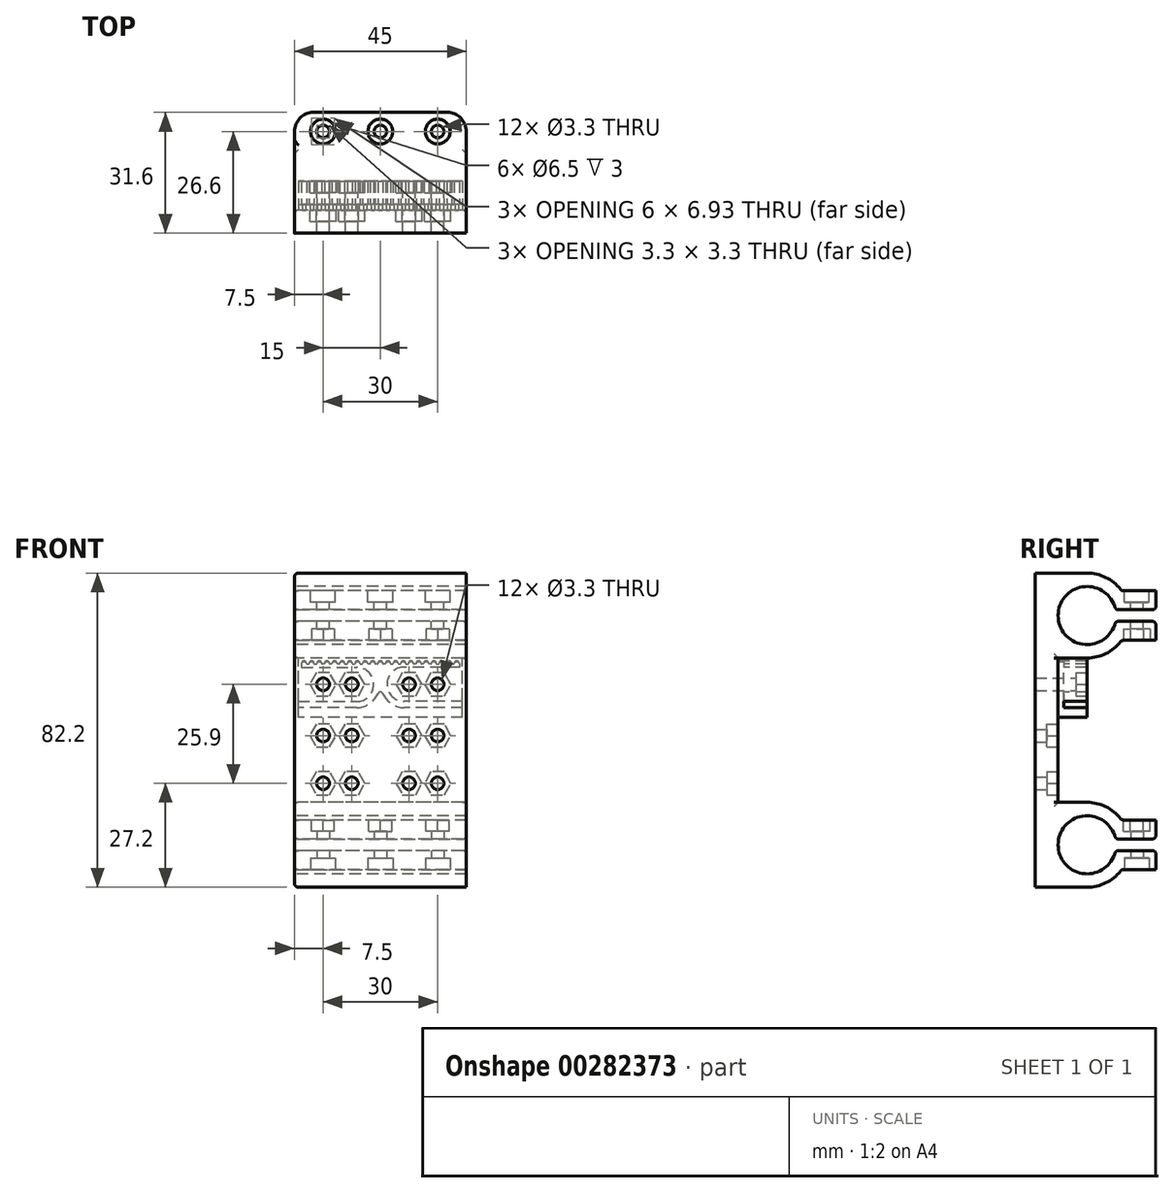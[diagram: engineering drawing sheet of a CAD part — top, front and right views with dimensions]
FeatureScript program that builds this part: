
annotation { "Feature Type Name" : "Feature", "Feature Type Description" : "" }
export const myFeature = defineFeature(function(context is Context, id is Id, definition is map)
    precondition{}
    {
        {
            var Q0;
            Q0=qCreatedBy(makeId("Right.planeOp"),FACE);
            var sketch = newSketch(context, id + "F0", { "sketchPlane" : qUnion([Q0])});
            skLineSegment(sketch, "E0.bottom", {"start": v(0, 0) * mm, "end": v(13.6, 0) * mm});
            skLineSegment(sketch, "E0.top", {"start": v(0, 82.2) * mm, "end": v(13.6, 82.2) * mm});
            skLineSegment(sketch, "E0.left", {"start": v(0, 0) * mm, "end": v(0, 82.2) * mm});
            skLineSegment(sketch, "E0.right", {"start": v(6, 22.2) * mm, "end": v(6, 60) * mm});
            skArc(sketch, "E1", {"start": v(21.05, 72.6) * mm, "mid": v(6, 71.1) * mm, "end": v(21.05, 69.6) * mm});
            skArc(sketch, "E2", {"start": v(21.05, 12.6) * mm, "mid": v(6, 11.1) * mm, "end": v(21.05, 9.6) * mm});
            skLineSegment(sketch, "E3", {"start": v(13.6, 71.1) * mm, "end": v(13.6, 11.1) * mm, "construction": true});
            skLineSegment(sketch, "E4", {"start": v(6, 41.1) * mm, "end": v(13.6, 41.1) * mm, "construction": true});
            skArc(sketch, "E5", {"start": v(13.6, 60) * mm, "mid": v(18.65, 61.22) * mm, "end": v(22.6, 64.6) * mm});
            skArc(sketch, "E6", {"start": v(13.6, 0) * mm, "mid": v(18.65, 1.22) * mm, "end": v(22.6, 4.6) * mm});
            skPoint(sketch, "E7.orphan", {"position": v(6, 82.2) * mm});
            skPoint(sketch, "E8.orphan", {"position": v(6, 0) * mm});
            skLineSegment(sketch, "E9", {"start": v(13.6, 22.2) * mm, "end": v(6, 22.2) * mm});
            skLineSegment(sketch, "E10", {"start": v(13.6, 60) * mm, "end": v(6, 60) * mm});
            skLineSegment(sketch, "E11", {"start": v(13.6, 11.1) * mm, "end": v(31.6, 11.1) * mm, "construction": true});
            skLineSegment(sketch, "E12", {"start": v(13.6, 71.1) * mm, "end": v(31.6, 71.1) * mm, "construction": true});
            skLineSegment(sketch, "E13.0", {"start": v(21.05, 9.6) * mm, "end": v(31.6, 9.6) * mm});
            skLineSegment(sketch, "E14.0", {"start": v(21.05, 12.6) * mm, "end": v(31.6, 12.6) * mm});
            skLineSegment(sketch, "E15.0", {"start": v(22.6, 4.6) * mm, "end": v(31.6, 4.6) * mm});
            skLineSegment(sketch, "E16.0", {"start": v(22.6, 17.6) * mm, "end": v(31.6, 17.6) * mm});
            skLineSegment(sketch, "E17", {"start": v(31.6, 17.6) * mm, "end": v(31.6, 12.6) * mm});
            skLineSegment(sketch, "E18", {"start": v(31.6, 9.6) * mm, "end": v(31.6, 4.6) * mm});
            skLineSegment(sketch, "E19", {"start": v(31.6, 12.6) * mm, "end": v(31.6, 11.1) * mm, "construction": true});
            skLineSegment(sketch, "E20", {"start": v(31.6, 9.6) * mm, "end": v(31.6, 11.1) * mm, "construction": true});
            skArc(sketch, "E21.trimOffspring", {"start": v(22.6, 17.6) * mm, "mid": v(18.65, 20.98) * mm, "end": v(13.6, 22.2) * mm});
            skLineSegment(sketch, "E22.0", {"start": v(21.05, 69.6) * mm, "end": v(31.6, 69.6) * mm});
            skLineSegment(sketch, "E23.0", {"start": v(21.05, 72.6) * mm, "end": v(31.6, 72.6) * mm});
            skLineSegment(sketch, "E24.0", {"start": v(22.6, 77.6) * mm, "end": v(31.6, 77.6) * mm});
            skLineSegment(sketch, "E25.0", {"start": v(22.6, 64.6) * mm, "end": v(31.6, 64.6) * mm});
            skLineSegment(sketch, "E26", {"start": v(31.6, 64.6) * mm, "end": v(31.6, 69.6) * mm});
            skLineSegment(sketch, "E27", {"start": v(31.6, 77.6) * mm, "end": v(31.6, 72.6) * mm});
            skLineSegment(sketch, "E28", {"start": v(31.6, 69.6) * mm, "end": v(31.6, 71.1) * mm, "construction": true});
            skLineSegment(sketch, "E29", {"start": v(31.6, 72.6) * mm, "end": v(31.6, 71.1) * mm, "construction": true});
            skArc(sketch, "E30.trimOffspring", {"start": v(22.6, 77.6) * mm, "mid": v(18.65, 80.98) * mm, "end": v(13.6, 82.2) * mm});
            skSolve(sketch);
        }
        {
            var Q0;
            Q0=qSketchRegion(id+"F0",true);
            extrude(context, id + "F1", {"entities" : qUnion([Q0]), "depth" : 45 * mm});
        }
        {
            var Q0;
            Q0=makeQuery(id+"F1.opExtrude","CAP_EDGE",EDGE,{"disambiguationData":[OSD([sQuery(id+"F0.wireOp",EDGE,"E0.right")])],"isStart":true});
            var Q1;
            Q1=makeQuery(id+"F1.opExtrude","CAP_EDGE",EDGE,{"disambiguationData":[OSD([sQuery(id+"F0.wireOp",EDGE,"E0.right")])],"isStart":false});
            fillet(context, id + "F2", {"entities" : qUnion([Q0, Q1]), "radius" : 1 * mm, "tangentPropagation" : true, "allowEdgeOverflow" : false});
        }
        {
            var Q0;
            Q0=makeQuery(id+"F1.opExtrude","SWEPT_FACE",FACE,{"disambiguationData":[OSD([sQuery(id+"F0.wireOp",EDGE,"E0.right")])]});
            var sketch = newSketch(context, id + "F3", { "sketchPlane" : qUnion([Q0])});
            skLineSegment(sketch, "E31.bottom", {"start": v(-43.15, 57.6) * mm, "end": v(-28.75, 57.6) * mm});
            skLineSegment(sketch, "E31.top", {"start": v(-44, 48.6) * mm, "end": v(-28.75, 48.6) * mm});
            skLineSegment(sketch, "E31.left", {"start": v(-44, 60) * mm, "end": v(-44, 48.6) * mm});
            skLineSegment(sketch, "E31.right", {"start": v(-28.75, 57.6) * mm, "end": v(-28.75, 48.6) * mm, "construction": true});
            skLineSegment(sketch, "E32.bottom", {"start": v(-1, 48.6) * mm, "end": v(-16.25, 48.6) * mm});
            skLineSegment(sketch, "E32.top", {"start": v(-1.85, 57.6) * mm, "end": v(-16.25, 57.6) * mm});
            skLineSegment(sketch, "E32.left", {"start": v(-1, 48.6) * mm, "end": v(-1, 60) * mm});
            skLineSegment(sketch, "E32.right", {"start": v(-16.25, 48.6) * mm, "end": v(-16.25, 57.6) * mm, "construction": true});
            skArc(sketch, "E33", {"start": v(-28.75, 48.6) * mm, "mid": v(-24.25, 53.1) * mm, "end": v(-28.75, 57.6) * mm});
            skArc(sketch, "E34", {"start": v(-16.25, 57.6) * mm, "mid": v(-20.75, 53.1) * mm, "end": v(-16.25, 48.6) * mm});
            skLineSegment(sketch, "E35", {"start": v(-28.75, 53.1) * mm, "end": v(-16.25, 53.1) * mm, "construction": true});
            skLineSegment(sketch, "E36", {"start": v(-22.5, 60) * mm, "end": v(-22.5, 53.1) * mm, "construction": true});
            skLineSegment(sketch, "E37.bottom", {"start": v(-44, 60) * mm, "end": v(-1, 60) * mm});
            skLineSegment(sketch, "E37.top", {"start": v(-44, 59.2) * mm, "end": v(-1, 59.2) * mm, "construction": true});
            skLineSegment(sketch, "E38.bottom", {"start": v(-44, 47) * mm, "end": v(-28.75, 47) * mm});
            skLineSegment(sketch, "E38.top", {"start": v(-44, 44.5) * mm, "end": v(-1, 44.5) * mm});
            skLineSegment(sketch, "E38.left", {"start": v(-44, 47) * mm, "end": v(-44, 44.5) * mm});
            skLineSegment(sketch, "E39", {"start": v(-1, 47) * mm, "end": v(-1, 44.5) * mm});
            skLineSegment(sketch, "E40", {"start": v(-25.5, 58.45) * mm, "end": v(-25.25, 58.45) * mm});
            skLineSegment(sketch, "E41", {"start": v(-20.5, 60) * mm, "end": v(-20.5, 53.1) * mm, "construction": true});
            skLineSegment(sketch, "E42", {"start": v(-24.5, 60) * mm, "end": v(-24.5, 53.1) * mm, "construction": true});
            skLineSegment(sketch, "E43", {"start": v(-25.15, 58.55) * mm, "end": v(-19.85, 58.55) * mm, "construction": true});
            skArc(sketch, "E44", {"start": v(-23.85, 58.55) * mm, "mid": v(-24.5, 59.2) * mm, "end": v(-25.15, 58.55) * mm});
            skArc(sketch, "E45", {"start": v(-21.85, 58.55) * mm, "mid": v(-22.5, 59.2) * mm, "end": v(-23.15, 58.55) * mm});
            skArc(sketch, "E46", {"start": v(-19.85, 58.55) * mm, "mid": v(-20.5, 59.2) * mm, "end": v(-21.15, 58.55) * mm});
            skLineSegment(sketch, "E47", {"start": v(-19.85, 58.55) * mm, "end": v(-19.85, 58.55) * mm});
            skLineSegment(sketch, "E48", {"start": v(-21.15, 58.55) * mm, "end": v(-21.15, 58.55) * mm});
            skLineSegment(sketch, "E49", {"start": v(-21.85, 58.55) * mm, "end": v(-21.85, 58.55) * mm});
            skLineSegment(sketch, "E50", {"start": v(-23.15, 58.55) * mm, "end": v(-23.15, 58.55) * mm});
            skLineSegment(sketch, "E51", {"start": v(-23.85, 58.55) * mm, "end": v(-23.85, 58.55) * mm});
            skLineSegment(sketch, "E52", {"start": v(-25.15, 58.55) * mm, "end": v(-25.15, 58.55) * mm});
            skLineSegment(sketch, "E53.trimOffspring", {"start": v(-21.75, 58.45) * mm, "end": v(-21.25, 58.45) * mm});
            skLineSegment(sketch, "E54.trimOffspring", {"start": v(-23.75, 58.45) * mm, "end": v(-23.25, 58.45) * mm});
            skLineSegment(sketch, "E55.trimOffspring", {"start": v(-19.75, 58.45) * mm, "end": v(-19.5, 58.45) * mm});
            skPoint(sketch, "E56.visualSharp", {"position": v(-23.85, 58.45) * mm});
            skArc(sketch, "E56.filletArc", {"start": v(-23.85, 58.55) * mm, "mid": v(-23.82, 58.48) * mm, "end": v(-23.75, 58.45) * mm});
            skPoint(sketch, "E57.visualSharp", {"position": v(-23.15, 58.45) * mm});
            skArc(sketch, "E57.filletArc", {"start": v(-23.25, 58.45) * mm, "mid": v(-23.18, 58.48) * mm, "end": v(-23.15, 58.55) * mm});
            skPoint(sketch, "E58.visualSharp", {"position": v(-21.85, 58.45) * mm});
            skArc(sketch, "E58.filletArc", {"start": v(-21.85, 58.55) * mm, "mid": v(-21.82, 58.48) * mm, "end": v(-21.75, 58.45) * mm});
            skPoint(sketch, "E59.visualSharp", {"position": v(-21.15, 58.45) * mm});
            skArc(sketch, "E59.filletArc", {"start": v(-21.25, 58.45) * mm, "mid": v(-21.18, 58.48) * mm, "end": v(-21.15, 58.55) * mm});
            skPoint(sketch, "E60.visualSharp", {"position": v(-25.15, 58.45) * mm});
            skArc(sketch, "E60.filletArc", {"start": v(-25.25, 58.45) * mm, "mid": v(-25.18, 58.48) * mm, "end": v(-25.15, 58.55) * mm});
            skPoint(sketch, "E61.visualSharp", {"position": v(-19.85, 58.45) * mm});
            skArc(sketch, "E61.filletArc", {"start": v(-19.85, 58.55) * mm, "mid": v(-19.82, 58.48) * mm, "end": v(-19.75, 58.45) * mm});
            skLineSegment(sketch, "E62", {"start": v(-25.5, 60) * mm, "end": v(-25.5, 53.1) * mm, "construction": true});
            skLineSegment(sketch, "E63", {"start": v(-19.5, 60) * mm, "end": v(-19.5, 53.1) * mm, "construction": true});
            skLineSegment(sketch, "E64.MirrorCS", {"start": v(-25.5, 58.45) * mm, "end": v(-25.75, 58.45) * mm});
            skPoint(sketch, "E65.MirrorP", {"position": v(-25.85, 58.45) * mm});
            skArc(sketch, "E66.MirrorCS", {"start": v(-25.75, 58.45) * mm, "mid": v(-25.82, 58.48) * mm, "end": v(-25.85, 58.55) * mm});
            skArc(sketch, "E67.MirrorCS", {"start": v(-27.15, 58.55) * mm, "mid": v(-26.5, 59.2) * mm, "end": v(-25.85, 58.55) * mm});
            skArc(sketch, "E68.MirrorCS", {"start": v(-27.15, 58.55) * mm, "mid": v(-27.18, 58.48) * mm, "end": v(-27.25, 58.45) * mm});
            skLineSegment(sketch, "E69.MirrorCS", {"start": v(-27.25, 58.45) * mm, "end": v(-27.75, 58.45) * mm});
            skArc(sketch, "E70.MirrorCS", {"start": v(-27.75, 58.45) * mm, "mid": v(-27.82, 58.48) * mm, "end": v(-27.85, 58.55) * mm});
            skArc(sketch, "E71.MirrorCS", {"start": v(-29.15, 58.55) * mm, "mid": v(-28.5, 59.2) * mm, "end": v(-27.85, 58.55) * mm});
            skArc(sketch, "E72.MirrorCS", {"start": v(-29.15, 58.55) * mm, "mid": v(-29.18, 58.48) * mm, "end": v(-29.25, 58.45) * mm});
            skLineSegment(sketch, "E73.MirrorCS", {"start": v(-29.25, 58.45) * mm, "end": v(-29.75, 58.45) * mm});
            skArc(sketch, "E74.MirrorCS", {"start": v(-29.75, 58.45) * mm, "mid": v(-29.82, 58.48) * mm, "end": v(-29.85, 58.55) * mm});
            skArc(sketch, "E75.MirrorCS", {"start": v(-31.15, 58.55) * mm, "mid": v(-30.5, 59.2) * mm, "end": v(-29.85, 58.55) * mm});
            skArc(sketch, "E76.MirrorCS", {"start": v(-31.15, 58.55) * mm, "mid": v(-31.18, 58.48) * mm, "end": v(-31.25, 58.45) * mm});
            skLineSegment(sketch, "E77.MirrorCS", {"start": v(-31.25, 58.45) * mm, "end": v(-31.5, 58.45) * mm});
            skLineSegment(sketch, "E78.MirrorCS", {"start": v(-19.25, 58.45) * mm, "end": v(-19.5, 58.45) * mm});
            skArc(sketch, "E79.MirrorCS", {"start": v(-19.15, 58.55) * mm, "mid": v(-19.18, 58.48) * mm, "end": v(-19.25, 58.45) * mm});
            skArc(sketch, "E80.MirrorCS", {"start": v(-19.15, 58.55) * mm, "mid": v(-18.5, 59.2) * mm, "end": v(-17.85, 58.55) * mm});
            skArc(sketch, "E81.MirrorCS", {"start": v(-17.75, 58.45) * mm, "mid": v(-17.82, 58.48) * mm, "end": v(-17.85, 58.55) * mm});
            skLineSegment(sketch, "E82.MirrorCS", {"start": v(-17.25, 58.45) * mm, "end": v(-17.75, 58.45) * mm});
            skPoint(sketch, "E83.MirrorP", {"position": v(-17.15, 58.45) * mm});
            skArc(sketch, "E84.MirrorCS", {"start": v(-17.15, 58.55) * mm, "mid": v(-17.18, 58.48) * mm, "end": v(-17.25, 58.45) * mm});
            skArc(sketch, "E85.MirrorCS", {"start": v(-17.15, 58.55) * mm, "mid": v(-16.5, 59.2) * mm, "end": v(-15.85, 58.55) * mm});
            skArc(sketch, "E86.MirrorCS", {"start": v(-15.75, 58.45) * mm, "mid": v(-15.82, 58.48) * mm, "end": v(-15.85, 58.55) * mm});
            skLineSegment(sketch, "E87.MirrorCS", {"start": v(-15.25, 58.45) * mm, "end": v(-15.75, 58.45) * mm});
            skArc(sketch, "E88.MirrorCS", {"start": v(-15.15, 58.55) * mm, "mid": v(-15.18, 58.48) * mm, "end": v(-15.25, 58.45) * mm});
            skArc(sketch, "E89.MirrorCS", {"start": v(-15.15, 58.55) * mm, "mid": v(-14.5, 59.2) * mm, "end": v(-13.85, 58.55) * mm});
            skArc(sketch, "E90.MirrorCS", {"start": v(-13.75, 58.45) * mm, "mid": v(-13.82, 58.48) * mm, "end": v(-13.85, 58.55) * mm});
            skLineSegment(sketch, "E91.MirrorCS", {"start": v(-13.5, 58.45) * mm, "end": v(-13.75, 58.45) * mm});
            skLineSegment(sketch, "E92.MirrorCS", {"start": v(-13.5, 58.45) * mm, "end": v(-13.25, 58.45) * mm});
            skArc(sketch, "E93.MirrorCS", {"start": v(-13.25, 58.45) * mm, "mid": v(-13.18, 58.48) * mm, "end": v(-13.15, 58.55) * mm});
            skArc(sketch, "E94.MirrorCS", {"start": v(-11.85, 58.55) * mm, "mid": v(-12.5, 59.2) * mm, "end": v(-13.15, 58.55) * mm});
            skArc(sketch, "E95.MirrorCS", {"start": v(-11.85, 58.55) * mm, "mid": v(-11.82, 58.48) * mm, "end": v(-11.75, 58.45) * mm});
            skLineSegment(sketch, "E96.MirrorCS", {"start": v(-11.75, 58.45) * mm, "end": v(-11.25, 58.45) * mm});
            skArc(sketch, "E97.MirrorCS", {"start": v(-11.25, 58.45) * mm, "mid": v(-11.18, 58.48) * mm, "end": v(-11.15, 58.55) * mm});
            skArc(sketch, "E98.MirrorCS", {"start": v(-9.85, 58.55) * mm, "mid": v(-10.5, 59.2) * mm, "end": v(-11.15, 58.55) * mm});
            skArc(sketch, "E99.MirrorCS", {"start": v(-9.85, 58.55) * mm, "mid": v(-9.82, 58.48) * mm, "end": v(-9.75, 58.45) * mm});
            skLineSegment(sketch, "E100.MirrorCS", {"start": v(-9.75, 58.45) * mm, "end": v(-9.25, 58.45) * mm});
            skArc(sketch, "E101.MirrorCS", {"start": v(-9.25, 58.45) * mm, "mid": v(-9.18, 58.48) * mm, "end": v(-9.15, 58.55) * mm});
            skArc(sketch, "E102.MirrorCS", {"start": v(-7.85, 58.55) * mm, "mid": v(-8.5, 59.2) * mm, "end": v(-9.15, 58.55) * mm});
            skArc(sketch, "E103.MirrorCS", {"start": v(-7.85, 58.55) * mm, "mid": v(-7.82, 58.48) * mm, "end": v(-7.75, 58.45) * mm});
            skLineSegment(sketch, "E104.MirrorCS", {"start": v(-7.75, 58.45) * mm, "end": v(-7.5, 58.45) * mm});
            skLineSegment(sketch, "E105", {"start": v(-28.75, 53.1) * mm, "end": v(-31.5, 53.1) * mm, "construction": true});
            skLineSegment(sketch, "E106", {"start": v(-31.5, 53.1) * mm, "end": v(-31.5, 60) * mm, "construction": true});
            skLineSegment(sketch, "E107.MirrorCS", {"start": v(-31.75, 58.45) * mm, "end": v(-31.5, 58.45) * mm});
            skArc(sketch, "E108.MirrorCS", {"start": v(-31.85, 58.55) * mm, "mid": v(-31.82, 58.48) * mm, "end": v(-31.75, 58.45) * mm});
            skArc(sketch, "E109.MirrorCS", {"start": v(-31.85, 58.55) * mm, "mid": v(-32.5, 59.2) * mm, "end": v(-33.15, 58.55) * mm});
            skArc(sketch, "E110.MirrorCS", {"start": v(-33.25, 58.45) * mm, "mid": v(-33.18, 58.48) * mm, "end": v(-33.15, 58.55) * mm});
            skLineSegment(sketch, "E111.MirrorCS", {"start": v(-33.75, 58.45) * mm, "end": v(-33.25, 58.45) * mm});
            skArc(sketch, "E112.MirrorCS", {"start": v(-33.85, 58.55) * mm, "mid": v(-33.82, 58.48) * mm, "end": v(-33.75, 58.45) * mm});
            skArc(sketch, "E113.MirrorCS", {"start": v(-33.85, 58.55) * mm, "mid": v(-34.5, 59.2) * mm, "end": v(-35.15, 58.55) * mm});
            skArc(sketch, "E114.MirrorCS", {"start": v(-35.25, 58.45) * mm, "mid": v(-35.18, 58.48) * mm, "end": v(-35.15, 58.55) * mm});
            skLineSegment(sketch, "E115.MirrorCS", {"start": v(-35.75, 58.45) * mm, "end": v(-35.25, 58.45) * mm});
            skArc(sketch, "E116.MirrorCS", {"start": v(-35.85, 58.55) * mm, "mid": v(-35.82, 58.48) * mm, "end": v(-35.75, 58.45) * mm});
            skArc(sketch, "E117.MirrorCS", {"start": v(-35.85, 58.55) * mm, "mid": v(-36.5, 59.2) * mm, "end": v(-37.15, 58.55) * mm});
            skArc(sketch, "E118.MirrorCS", {"start": v(-37.25, 58.45) * mm, "mid": v(-37.18, 58.48) * mm, "end": v(-37.15, 58.55) * mm});
            skLineSegment(sketch, "E119.MirrorCS", {"start": v(-37.5, 58.45) * mm, "end": v(-37.25, 58.45) * mm});
            skLineSegment(sketch, "E120.MirrorCS", {"start": v(-37.5, 58.45) * mm, "end": v(-37.75, 58.45) * mm});
            skArc(sketch, "E121.MirrorCS", {"start": v(-37.75, 58.45) * mm, "mid": v(-37.82, 58.48) * mm, "end": v(-37.85, 58.55) * mm});
            skArc(sketch, "E122.MirrorCS", {"start": v(-39.15, 58.55) * mm, "mid": v(-38.5, 59.2) * mm, "end": v(-37.85, 58.55) * mm});
            skArc(sketch, "E123.MirrorCS", {"start": v(-39.15, 58.55) * mm, "mid": v(-39.18, 58.48) * mm, "end": v(-39.25, 58.45) * mm});
            skLineSegment(sketch, "E124.MirrorCS", {"start": v(-39.25, 58.45) * mm, "end": v(-39.75, 58.45) * mm});
            skArc(sketch, "E125.MirrorCS", {"start": v(-39.75, 58.45) * mm, "mid": v(-39.82, 58.48) * mm, "end": v(-39.85, 58.55) * mm});
            skArc(sketch, "E126.MirrorCS", {"start": v(-41.15, 58.55) * mm, "mid": v(-40.5, 59.2) * mm, "end": v(-39.85, 58.55) * mm});
            skArc(sketch, "E127.MirrorCS", {"start": v(-41.15, 58.55) * mm, "mid": v(-41.18, 58.48) * mm, "end": v(-41.25, 58.45) * mm});
            skLineSegment(sketch, "E128.MirrorCS", {"start": v(-41.25, 58.45) * mm, "end": v(-41.75, 58.45) * mm});
            skArc(sketch, "E129.MirrorCS", {"start": v(-41.75, 58.45) * mm, "mid": v(-41.82, 58.48) * mm, "end": v(-41.85, 58.55) * mm});
            skArc(sketch, "E130.MirrorCS", {"start": v(-43.15, 58.55) * mm, "mid": v(-42.5, 59.2) * mm, "end": v(-41.85, 58.55) * mm});
            skLineSegment(sketch, "E131", {"start": v(-16.25, 53.1) * mm, "end": v(-7.5, 53.1) * mm, "construction": true});
            skLineSegment(sketch, "E132", {"start": v(-7.5, 53.1) * mm, "end": v(-7.5, 58.45) * mm, "construction": true});
            skLineSegment(sketch, "E133", {"start": v(-7.5, 60) * mm, "end": v(-7.5, 58.45) * mm, "construction": true});
            skLineSegment(sketch, "E134.MirrorCS", {"start": v(-7.25, 58.45) * mm, "end": v(-7.5, 58.45) * mm});
            skArc(sketch, "E135.MirrorCS", {"start": v(-7.15, 58.55) * mm, "mid": v(-7.18, 58.48) * mm, "end": v(-7.25, 58.45) * mm});
            skArc(sketch, "E136.MirrorCS", {"start": v(-7.15, 58.55) * mm, "mid": v(-6.5, 59.2) * mm, "end": v(-5.85, 58.55) * mm});
            skArc(sketch, "E137.MirrorCS", {"start": v(-5.75, 58.45) * mm, "mid": v(-5.82, 58.48) * mm, "end": v(-5.85, 58.55) * mm});
            skLineSegment(sketch, "E138.MirrorCS", {"start": v(-5.25, 58.45) * mm, "end": v(-5.75, 58.45) * mm});
            skArc(sketch, "E139.MirrorCS", {"start": v(-5.15, 58.55) * mm, "mid": v(-5.18, 58.48) * mm, "end": v(-5.25, 58.45) * mm});
            skArc(sketch, "E140.MirrorCS", {"start": v(-5.15, 58.55) * mm, "mid": v(-4.5, 59.2) * mm, "end": v(-3.85, 58.55) * mm});
            skArc(sketch, "E141.MirrorCS", {"start": v(-3.75, 58.45) * mm, "mid": v(-3.82, 58.48) * mm, "end": v(-3.85, 58.55) * mm});
            skLineSegment(sketch, "E142.MirrorCS", {"start": v(-3.25, 58.45) * mm, "end": v(-3.75, 58.45) * mm});
            skArc(sketch, "E143.MirrorCS", {"start": v(-3.15, 58.55) * mm, "mid": v(-3.18, 58.48) * mm, "end": v(-3.25, 58.45) * mm});
            skArc(sketch, "E144.MirrorCS", {"start": v(-3.15, 58.55) * mm, "mid": v(-2.5, 59.2) * mm, "end": v(-1.85, 58.55) * mm});
            skLineSegment(sketch, "E145", {"start": v(-1.85, 58.55) * mm, "end": v(-1.85, 57.6) * mm});
            skLineSegment(sketch, "E146", {"start": v(-43.15, 58.55) * mm, "end": v(-43.15, 57.6) * mm});
            skLineSegment(sketch, "E147", {"start": v(-22.5, 53.1) * mm, "end": v(-22.5, 47) * mm, "construction": true});
            skArc(sketch, "E148.0", {"start": v(-21.82, 50.6) * mm, "mid": v(-19.57, 47.98) * mm, "end": v(-16.25, 47) * mm});
            skArc(sketch, "E149.0", {"start": v(-28.75, 47) * mm, "mid": v(-25.43, 47.98) * mm, "end": v(-23.18, 50.6) * mm});
            skLineSegment(sketch, "E150.trimOffspring", {"start": v(-16.25, 47) * mm, "end": v(-1, 47) * mm});
            skArc(sketch, "E151", {"start": v(-21.82, 50.6) * mm, "mid": v(-22.5, 51.05) * mm, "end": v(-23.18, 50.6) * mm});
            skLineSegment(sketch, "E152", {"start": v(-28.75, 47) * mm, "end": v(-22.5, 47) * mm, "construction": true});
            skLineSegment(sketch, "E153", {"start": v(-16.25, 47) * mm, "end": v(-22.5, 47) * mm, "construction": true});
            skSolve(sketch);
        }
        {
            var Q0;
            Q0=qSketchRegion(id+"F3",true);
            extrude(context, id + "F4", {"entities" : qUnion([Q0]), "operationType" : NewBodyOperationType.ADD, "depth" : 7.6 * mm});
        }
        {
            var Q0;
            {var subQ0=sQuery(id+"F0.wireOp",EDGE,"E0.right");Q0=makeQuery(id+"F4.boolean.opBoolean","SPLIT",FACE,{"disambiguationData":[TD([makeQuery(id+"F4.opExtrude","SWEPT_FACE",FACE,{"disambiguationData":[OSD([sQuery(id+"F3.wireOp",EDGE,"E31.bottom")])]})])],"derivedFrom":makeQuery(id+"F1.opExtrude","SWEPT_FACE",FACE,{"disambiguationData":[OSD([subQ0])]})});}
            var sketch = newSketch(context, id + "F5", { "sketchPlane" : qUnion([Q0])});
            skLineSegment(sketch, "E154.bottom", {"start": v(-44, 47) * mm, "end": v(-1, 47) * mm});
            skLineSegment(sketch, "E154.top", {"start": v(-44, 59) * mm, "end": v(-1, 59) * mm});
            skLineSegment(sketch, "E154.left", {"start": v(-44, 47) * mm, "end": v(-44, 59) * mm});
            skLineSegment(sketch, "E154.right", {"start": v(-1, 47) * mm, "end": v(-1, 59) * mm});
            skSolve(sketch);
        }
        {
            var Q0;
            Q0=qSketchRegion(id+"F5",true);
            extrude(context, id + "F6", {"entities" : qUnion([Q0]), "operationType" : NewBodyOperationType.ADD, "depth" : 1.5 * mm});
        }
        {
            var Q0;
            Q0=makeQuery(id+"F4.opExtrude","CAP_FACE",FACE,{"disambiguationData":[OSD([sQuery(id+"F3.wireOp",EDGE,"E31.bottom"),sQuery(id+"F3.wireOp",EDGE,"E31.top"),sQuery(id+"F3.wireOp",EDGE,"E31.left"),sQuery(id+"F3.wireOp",EDGE,"E32.bottom"),sQuery(id+"F3.wireOp",EDGE,"E32.top"),sQuery(id+"F3.wireOp",EDGE,"E32.left"),sQuery(id+"F3.wireOp",EDGE,"E33"),sQuery(id+"F3.wireOp",EDGE,"E34"),sQuery(id+"F3.wireOp",EDGE,"E37.bottom"),sQuery(id+"F3.wireOp",EDGE,"E40"),sQuery(id+"F3.wireOp",EDGE,"E44"),sQuery(id+"F3.wireOp",EDGE,"E45"),sQuery(id+"F3.wireOp",EDGE,"E46"),sQuery(id+"F3.wireOp",EDGE,"E53.trimOffspring"),sQuery(id+"F3.wireOp",EDGE,"E54.trimOffspring"),sQuery(id+"F3.wireOp",EDGE,"E55.trimOffspring"),sQuery(id+"F3.wireOp",EDGE,"E56.filletArc"),sQuery(id+"F3.wireOp",EDGE,"E57.filletArc"),sQuery(id+"F3.wireOp",EDGE,"E58.filletArc"),sQuery(id+"F3.wireOp",EDGE,"E59.filletArc"),sQuery(id+"F3.wireOp",EDGE,"E60.filletArc"),sQuery(id+"F3.wireOp",EDGE,"E61.filletArc"),sQuery(id+"F3.wireOp",EDGE,"E64.MirrorCS"),sQuery(id+"F3.wireOp",EDGE,"E66.MirrorCS"),sQuery(id+"F3.wireOp",EDGE,"E67.MirrorCS"),sQuery(id+"F3.wireOp",EDGE,"E68.MirrorCS"),sQuery(id+"F3.wireOp",EDGE,"E69.MirrorCS"),sQuery(id+"F3.wireOp",EDGE,"E70.MirrorCS"),sQuery(id+"F3.wireOp",EDGE,"E71.MirrorCS"),sQuery(id+"F3.wireOp",EDGE,"E72.MirrorCS"),sQuery(id+"F3.wireOp",EDGE,"E73.MirrorCS"),sQuery(id+"F3.wireOp",EDGE,"E74.MirrorCS"),sQuery(id+"F3.wireOp",EDGE,"E75.MirrorCS"),sQuery(id+"F3.wireOp",EDGE,"E76.MirrorCS"),sQuery(id+"F3.wireOp",EDGE,"E77.MirrorCS"),sQuery(id+"F3.wireOp",EDGE,"E78.MirrorCS"),sQuery(id+"F3.wireOp",EDGE,"E79.MirrorCS"),sQuery(id+"F3.wireOp",EDGE,"E80.MirrorCS"),sQuery(id+"F3.wireOp",EDGE,"E81.MirrorCS"),sQuery(id+"F3.wireOp",EDGE,"E82.MirrorCS"),sQuery(id+"F3.wireOp",EDGE,"E84.MirrorCS"),sQuery(id+"F3.wireOp",EDGE,"E85.MirrorCS"),sQuery(id+"F3.wireOp",EDGE,"E86.MirrorCS"),sQuery(id+"F3.wireOp",EDGE,"E87.MirrorCS"),sQuery(id+"F3.wireOp",EDGE,"E88.MirrorCS"),sQuery(id+"F3.wireOp",EDGE,"E89.MirrorCS"),sQuery(id+"F3.wireOp",EDGE,"E90.MirrorCS"),sQuery(id+"F3.wireOp",EDGE,"E91.MirrorCS"),sQuery(id+"F3.wireOp",EDGE,"E92.MirrorCS"),sQuery(id+"F3.wireOp",EDGE,"E93.MirrorCS"),sQuery(id+"F3.wireOp",EDGE,"E94.MirrorCS"),sQuery(id+"F3.wireOp",EDGE,"E95.MirrorCS"),sQuery(id+"F3.wireOp",EDGE,"E96.MirrorCS"),sQuery(id+"F3.wireOp",EDGE,"E97.MirrorCS"),sQuery(id+"F3.wireOp",EDGE,"E98.MirrorCS"),sQuery(id+"F3.wireOp",EDGE,"E99.MirrorCS"),sQuery(id+"F3.wireOp",EDGE,"E100.MirrorCS"),sQuery(id+"F3.wireOp",EDGE,"E101.MirrorCS"),sQuery(id+"F3.wireOp",EDGE,"E102.MirrorCS"),sQuery(id+"F3.wireOp",EDGE,"E103.MirrorCS"),sQuery(id+"F3.wireOp",EDGE,"E104.MirrorCS"),sQuery(id+"F3.wireOp",EDGE,"E107.MirrorCS"),sQuery(id+"F3.wireOp",EDGE,"E108.MirrorCS"),sQuery(id+"F3.wireOp",EDGE,"E109.MirrorCS"),sQuery(id+"F3.wireOp",EDGE,"E110.MirrorCS"),sQuery(id+"F3.wireOp",EDGE,"E111.MirrorCS"),sQuery(id+"F3.wireOp",EDGE,"E112.MirrorCS"),sQuery(id+"F3.wireOp",EDGE,"E113.MirrorCS"),sQuery(id+"F3.wireOp",EDGE,"E114.MirrorCS"),sQuery(id+"F3.wireOp",EDGE,"E115.MirrorCS"),sQuery(id+"F3.wireOp",EDGE,"E116.MirrorCS"),sQuery(id+"F3.wireOp",EDGE,"E117.MirrorCS"),sQuery(id+"F3.wireOp",EDGE,"E118.MirrorCS"),sQuery(id+"F3.wireOp",EDGE,"E119.MirrorCS"),sQuery(id+"F3.wireOp",EDGE,"E120.MirrorCS"),sQuery(id+"F3.wireOp",EDGE,"E121.MirrorCS"),sQuery(id+"F3.wireOp",EDGE,"E122.MirrorCS"),sQuery(id+"F3.wireOp",EDGE,"E123.MirrorCS"),sQuery(id+"F3.wireOp",EDGE,"E124.MirrorCS"),sQuery(id+"F3.wireOp",EDGE,"E125.MirrorCS"),sQuery(id+"F3.wireOp",EDGE,"E126.MirrorCS"),sQuery(id+"F3.wireOp",EDGE,"E127.MirrorCS"),sQuery(id+"F3.wireOp",EDGE,"E128.MirrorCS"),sQuery(id+"F3.wireOp",EDGE,"E129.MirrorCS"),sQuery(id+"F3.wireOp",EDGE,"E130.MirrorCS"),sQuery(id+"F3.wireOp",EDGE,"E134.MirrorCS"),sQuery(id+"F3.wireOp",EDGE,"E135.MirrorCS"),sQuery(id+"F3.wireOp",EDGE,"E136.MirrorCS"),sQuery(id+"F3.wireOp",EDGE,"E137.MirrorCS"),sQuery(id+"F3.wireOp",EDGE,"E138.MirrorCS"),sQuery(id+"F3.wireOp",EDGE,"E139.MirrorCS"),sQuery(id+"F3.wireOp",EDGE,"E140.MirrorCS"),sQuery(id+"F3.wireOp",EDGE,"E141.MirrorCS"),sQuery(id+"F3.wireOp",EDGE,"E142.MirrorCS"),sQuery(id+"F3.wireOp",EDGE,"E143.MirrorCS"),sQuery(id+"F3.wireOp",EDGE,"E144.MirrorCS"),sQuery(id+"F3.wireOp",EDGE,"E145"),sQuery(id+"F3.wireOp",EDGE,"E146")])],"isStart":false});
            var sketch = newSketch(context, id + "F7", { "sketchPlane" : qUnion([Q0])});
            skLineSegment(sketch, "E155", {"start": v(-37.5, 53.1) * mm, "end": v(-7.5, 53.1) * mm, "construction": true});
            skPoint(sketch, "E156.orphan", {"position": v(-28.75, 53.1) * mm});
            skLineSegment(sketch, "E157", {"start": v(-22.5, 58.55) * mm, "end": v(-22.5, 53.1) * mm, "construction": true});
            skPoint(sketch, "E158.orphan", {"position": v(-16.25, 53.1) * mm});
            skCircle(sketch, "E159.cCircle", {"center": v(-7.5, 53.1) * mm, "radius": 3 * mm, "construction": true});
            skLineSegment(sketch, "E159.0", {"start": v(-5.77, 50.1) * mm, "end": v(-9.23, 50.1) * mm});
            skLineSegment(sketch, "E159.1", {"start": v(-9.23, 50.1) * mm, "end": v(-10.96, 53.1) * mm});
            skLineSegment(sketch, "E159.2", {"start": v(-10.96, 53.1) * mm, "end": v(-9.23, 56.1) * mm});
            skLineSegment(sketch, "E159.3", {"start": v(-9.23, 56.1) * mm, "end": v(-5.77, 56.1) * mm});
            skLineSegment(sketch, "E159.4", {"start": v(-5.77, 56.1) * mm, "end": v(-4.04, 53.1) * mm});
            skLineSegment(sketch, "E159.5", {"start": v(-4.04, 53.1) * mm, "end": v(-5.77, 50.1) * mm});
            skPoint(sketch, "E159.0.midPoint", {"position": v(-7.5, 50.1) * mm});
            skCircle(sketch, "E160.cCircle", {"center": v(-37.5, 53.1) * mm, "radius": 3 * mm, "construction": true});
            skLineSegment(sketch, "E160.0", {"start": v(-35.77, 50.1) * mm, "end": v(-39.23, 50.1) * mm});
            skLineSegment(sketch, "E160.1", {"start": v(-39.23, 50.1) * mm, "end": v(-40.96, 53.1) * mm});
            skLineSegment(sketch, "E160.2", {"start": v(-40.96, 53.1) * mm, "end": v(-39.23, 56.1) * mm});
            skLineSegment(sketch, "E160.3", {"start": v(-39.23, 56.1) * mm, "end": v(-35.77, 56.1) * mm});
            skLineSegment(sketch, "E160.4", {"start": v(-35.77, 56.1) * mm, "end": v(-34.04, 53.1) * mm});
            skLineSegment(sketch, "E160.5", {"start": v(-34.04, 53.1) * mm, "end": v(-35.77, 50.1) * mm});
            skPoint(sketch, "E160.0.midPoint", {"position": v(-37.5, 50.1) * mm});
            skLineSegment(sketch, "E161", {"start": v(-37.5, 53.1) * mm, "end": v(-37.5, 50.1) * mm, "construction": true});
            skLineSegment(sketch, "E162", {"start": v(-7.5, 53.1) * mm, "end": v(-7.5, 50.1) * mm, "construction": true});
            skCircle(sketch, "E163.cCircle", {"center": v(-30, 53.1) * mm, "radius": 3 * mm, "construction": true});
            skLineSegment(sketch, "E163.0", {"start": v(-28.27, 50.1) * mm, "end": v(-31.73, 50.1) * mm});
            skLineSegment(sketch, "E163.1", {"start": v(-31.73, 50.1) * mm, "end": v(-33.46, 53.1) * mm});
            skLineSegment(sketch, "E163.2", {"start": v(-33.46, 53.1) * mm, "end": v(-31.73, 56.1) * mm});
            skLineSegment(sketch, "E163.3", {"start": v(-31.73, 56.1) * mm, "end": v(-28.27, 56.1) * mm});
            skLineSegment(sketch, "E163.4", {"start": v(-28.27, 56.1) * mm, "end": v(-26.54, 53.1) * mm});
            skLineSegment(sketch, "E163.5", {"start": v(-26.54, 53.1) * mm, "end": v(-28.27, 50.1) * mm});
            skPoint(sketch, "E163.0.midPoint", {"position": v(-30, 50.1) * mm});
            skCircle(sketch, "E164.cCircle", {"center": v(-15, 53.1) * mm, "radius": 3 * mm, "construction": true});
            skLineSegment(sketch, "E164.0", {"start": v(-13.27, 50.1) * mm, "end": v(-16.73, 50.1) * mm});
            skLineSegment(sketch, "E164.1", {"start": v(-16.73, 50.1) * mm, "end": v(-18.46, 53.1) * mm});
            skLineSegment(sketch, "E164.2", {"start": v(-18.46, 53.1) * mm, "end": v(-16.73, 56.1) * mm});
            skLineSegment(sketch, "E164.3", {"start": v(-16.73, 56.1) * mm, "end": v(-13.27, 56.1) * mm});
            skLineSegment(sketch, "E164.4", {"start": v(-13.27, 56.1) * mm, "end": v(-11.54, 53.1) * mm});
            skLineSegment(sketch, "E164.5", {"start": v(-11.54, 53.1) * mm, "end": v(-13.27, 50.1) * mm});
            skPoint(sketch, "E164.0.midPoint", {"position": v(-15, 50.1) * mm});
            skSolve(sketch);
        }
        {
            var Q0;
            Q0=qSketchRegion(id+"F7",true);
            extrude(context, id + "F8", {"entities" : qUnion([Q0]), "operationType" : NewBodyOperationType.REMOVE, "oppositeDirection" : true, "depth" : 3 * mm});
        }
        {
            var Q0;
            Q0=makeQuery(id+"F4.opExtrude","CAP_FACE",FACE,{"disambiguationData":[OSD([sQuery(id+"F3.wireOp",EDGE,"E31.bottom"),sQuery(id+"F3.wireOp",EDGE,"E31.top"),sQuery(id+"F3.wireOp",EDGE,"E31.left"),sQuery(id+"F3.wireOp",EDGE,"E32.bottom"),sQuery(id+"F3.wireOp",EDGE,"E32.top"),sQuery(id+"F3.wireOp",EDGE,"E32.left"),sQuery(id+"F3.wireOp",EDGE,"E33"),sQuery(id+"F3.wireOp",EDGE,"E34"),sQuery(id+"F3.wireOp",EDGE,"E37.bottom"),sQuery(id+"F3.wireOp",EDGE,"E40"),sQuery(id+"F3.wireOp",EDGE,"E44"),sQuery(id+"F3.wireOp",EDGE,"E45"),sQuery(id+"F3.wireOp",EDGE,"E46"),sQuery(id+"F3.wireOp",EDGE,"E53.trimOffspring"),sQuery(id+"F3.wireOp",EDGE,"E54.trimOffspring"),sQuery(id+"F3.wireOp",EDGE,"E55.trimOffspring"),sQuery(id+"F3.wireOp",EDGE,"E56.filletArc"),sQuery(id+"F3.wireOp",EDGE,"E57.filletArc"),sQuery(id+"F3.wireOp",EDGE,"E58.filletArc"),sQuery(id+"F3.wireOp",EDGE,"E59.filletArc"),sQuery(id+"F3.wireOp",EDGE,"E60.filletArc"),sQuery(id+"F3.wireOp",EDGE,"E61.filletArc"),sQuery(id+"F3.wireOp",EDGE,"E64.MirrorCS"),sQuery(id+"F3.wireOp",EDGE,"E66.MirrorCS"),sQuery(id+"F3.wireOp",EDGE,"E67.MirrorCS"),sQuery(id+"F3.wireOp",EDGE,"E68.MirrorCS"),sQuery(id+"F3.wireOp",EDGE,"E69.MirrorCS"),sQuery(id+"F3.wireOp",EDGE,"E70.MirrorCS"),sQuery(id+"F3.wireOp",EDGE,"E71.MirrorCS"),sQuery(id+"F3.wireOp",EDGE,"E72.MirrorCS"),sQuery(id+"F3.wireOp",EDGE,"E73.MirrorCS"),sQuery(id+"F3.wireOp",EDGE,"E74.MirrorCS"),sQuery(id+"F3.wireOp",EDGE,"E75.MirrorCS"),sQuery(id+"F3.wireOp",EDGE,"E76.MirrorCS"),sQuery(id+"F3.wireOp",EDGE,"E77.MirrorCS"),sQuery(id+"F3.wireOp",EDGE,"E78.MirrorCS"),sQuery(id+"F3.wireOp",EDGE,"E79.MirrorCS"),sQuery(id+"F3.wireOp",EDGE,"E80.MirrorCS"),sQuery(id+"F3.wireOp",EDGE,"E81.MirrorCS"),sQuery(id+"F3.wireOp",EDGE,"E82.MirrorCS"),sQuery(id+"F3.wireOp",EDGE,"E84.MirrorCS"),sQuery(id+"F3.wireOp",EDGE,"E85.MirrorCS"),sQuery(id+"F3.wireOp",EDGE,"E86.MirrorCS"),sQuery(id+"F3.wireOp",EDGE,"E87.MirrorCS"),sQuery(id+"F3.wireOp",EDGE,"E88.MirrorCS"),sQuery(id+"F3.wireOp",EDGE,"E89.MirrorCS"),sQuery(id+"F3.wireOp",EDGE,"E90.MirrorCS"),sQuery(id+"F3.wireOp",EDGE,"E91.MirrorCS"),sQuery(id+"F3.wireOp",EDGE,"E92.MirrorCS"),sQuery(id+"F3.wireOp",EDGE,"E93.MirrorCS"),sQuery(id+"F3.wireOp",EDGE,"E94.MirrorCS"),sQuery(id+"F3.wireOp",EDGE,"E95.MirrorCS"),sQuery(id+"F3.wireOp",EDGE,"E96.MirrorCS"),sQuery(id+"F3.wireOp",EDGE,"E97.MirrorCS"),sQuery(id+"F3.wireOp",EDGE,"E98.MirrorCS"),sQuery(id+"F3.wireOp",EDGE,"E99.MirrorCS"),sQuery(id+"F3.wireOp",EDGE,"E100.MirrorCS"),sQuery(id+"F3.wireOp",EDGE,"E101.MirrorCS"),sQuery(id+"F3.wireOp",EDGE,"E102.MirrorCS"),sQuery(id+"F3.wireOp",EDGE,"E103.MirrorCS"),sQuery(id+"F3.wireOp",EDGE,"E104.MirrorCS"),sQuery(id+"F3.wireOp",EDGE,"E107.MirrorCS"),sQuery(id+"F3.wireOp",EDGE,"E108.MirrorCS"),sQuery(id+"F3.wireOp",EDGE,"E109.MirrorCS"),sQuery(id+"F3.wireOp",EDGE,"E110.MirrorCS"),sQuery(id+"F3.wireOp",EDGE,"E111.MirrorCS"),sQuery(id+"F3.wireOp",EDGE,"E112.MirrorCS"),sQuery(id+"F3.wireOp",EDGE,"E113.MirrorCS"),sQuery(id+"F3.wireOp",EDGE,"E114.MirrorCS"),sQuery(id+"F3.wireOp",EDGE,"E115.MirrorCS"),sQuery(id+"F3.wireOp",EDGE,"E116.MirrorCS"),sQuery(id+"F3.wireOp",EDGE,"E117.MirrorCS"),sQuery(id+"F3.wireOp",EDGE,"E118.MirrorCS"),sQuery(id+"F3.wireOp",EDGE,"E119.MirrorCS"),sQuery(id+"F3.wireOp",EDGE,"E120.MirrorCS"),sQuery(id+"F3.wireOp",EDGE,"E121.MirrorCS"),sQuery(id+"F3.wireOp",EDGE,"E122.MirrorCS"),sQuery(id+"F3.wireOp",EDGE,"E123.MirrorCS"),sQuery(id+"F3.wireOp",EDGE,"E124.MirrorCS"),sQuery(id+"F3.wireOp",EDGE,"E125.MirrorCS"),sQuery(id+"F3.wireOp",EDGE,"E126.MirrorCS"),sQuery(id+"F3.wireOp",EDGE,"E127.MirrorCS"),sQuery(id+"F3.wireOp",EDGE,"E128.MirrorCS"),sQuery(id+"F3.wireOp",EDGE,"E129.MirrorCS"),sQuery(id+"F3.wireOp",EDGE,"E130.MirrorCS"),sQuery(id+"F3.wireOp",EDGE,"E134.MirrorCS"),sQuery(id+"F3.wireOp",EDGE,"E135.MirrorCS"),sQuery(id+"F3.wireOp",EDGE,"E136.MirrorCS"),sQuery(id+"F3.wireOp",EDGE,"E137.MirrorCS"),sQuery(id+"F3.wireOp",EDGE,"E138.MirrorCS"),sQuery(id+"F3.wireOp",EDGE,"E139.MirrorCS"),sQuery(id+"F3.wireOp",EDGE,"E140.MirrorCS"),sQuery(id+"F3.wireOp",EDGE,"E141.MirrorCS"),sQuery(id+"F3.wireOp",EDGE,"E142.MirrorCS"),sQuery(id+"F3.wireOp",EDGE,"E143.MirrorCS"),sQuery(id+"F3.wireOp",EDGE,"E144.MirrorCS"),sQuery(id+"F3.wireOp",EDGE,"E145"),sQuery(id+"F3.wireOp",EDGE,"E146")])],"isStart":false});
            var sketch = newSketch(context, id + "F9", { "sketchPlane" : qUnion([Q0])});
            skLineSegment(sketch, "E165", {"start": v(-40.96, 53.1) * mm, "end": v(-34.04, 53.1) * mm, "construction": true});
            skLineSegment(sketch, "E166", {"start": v(-10.96, 53.1) * mm, "end": v(-4.04, 53.1) * mm, "construction": true});
            skCircle(sketch, "E167", {"center": v(-37.5, 53.1) * mm, "radius": 1.65 * mm});
            skCircle(sketch, "E168", {"center": v(-7.5, 53.1) * mm, "radius": 1.65 * mm});
            skLineSegment(sketch, "E169", {"start": v(-33.46, 53.1) * mm, "end": v(-26.54, 53.1) * mm, "construction": true});
            skLineSegment(sketch, "E170", {"start": v(-26.54, 53.1) * mm, "end": v(-18.46, 53.1) * mm, "construction": true});
            skLineSegment(sketch, "E171", {"start": v(-18.46, 53.1) * mm, "end": v(-11.54, 53.1) * mm, "construction": true});
            skCircle(sketch, "E172", {"center": v(-30, 53.1) * mm, "radius": 1.65 * mm});
            skCircle(sketch, "E173", {"center": v(-15, 53.1) * mm, "radius": 1.65 * mm});
            skSolve(sketch);
        }
        {
            var Q0;
            Q0=qSketchRegion(id+"F9",true);
            extrude(context, id + "F10", {"entities" : qUnion([Q0]), "operationType" : NewBodyOperationType.REMOVE, "endBound" : BoundingType.THROUGH_ALL, "oppositeDirection" : true, "depth" : 25 * mm});
        }
        {
            var Q0;
            Q0=makeQuery(id+"F1.opExtrude","SWEPT_FACE",FACE,{"disambiguationData":[OSD([sQuery(id+"F0.wireOp",EDGE,"E24.0")])]});
            var sketch = newSketch(context, id + "F11", { "sketchPlane" : qUnion([Q0])});
            skLineSegment(sketch, "E174", {"start": v(0, 26.6) * mm, "end": v(45, 26.6) * mm, "construction": true});
            skLineSegment(sketch, "E175", {"start": v(22.5, 26.6) * mm, "end": v(22.5, 31.6) * mm, "construction": true});
            skPoint(sketch, "E176", {"position": v(7.5, 26.6) * mm});
            skPoint(sketch, "E177", {"position": v(37.5, 26.6) * mm});
            skPoint(sketch, "E178", {"position": v(22.5, 26.6) * mm});
            skSolve(sketch);
        }
        {
            var Q0;
            Q0=makeQuery(id+"F1.opExtrude","SWEPT_FACE",FACE,{"disambiguationData":[OSD([sQuery(id+"F0.wireOp",EDGE,"E15.0")])]});
            var sketch = newSketch(context, id + "F12", { "sketchPlane" : qUnion([Q0])});
            skLineSegment(sketch, "E179", {"start": v(0, -26.6) * mm, "end": v(45, -26.6) * mm, "construction": true});
            skLineSegment(sketch, "E180", {"start": v(22.5, -31.6) * mm, "end": v(22.5, -26.6) * mm, "construction": true});
            skPoint(sketch, "E181", {"position": v(7.5, -26.6) * mm});
            skPoint(sketch, "E182", {"position": v(37.5, -26.6) * mm});
            skPoint(sketch, "E183", {"position": v(22.5, -26.6) * mm});
            skSolve(sketch);
        }
        {
            var Q0;
            Q0=sQuery(id+"F11.wireOp",VERTEX,"E176");
            var Q1;
            Q1=sQuery(id+"F11.wireOp",VERTEX,"E177");
            var Q2;
            Q2=sQuery(id+"F12.wireOp",VERTEX,"E182");
            var Q3;
            Q3=sQuery(id+"F12.wireOp",VERTEX,"E181");
            var Q4;
            Q4=sQuery(id+"F12.wireOp",VERTEX,"E183");
            var Q5;
            Q5=sQuery(id+"F11.wireOp",VERTEX,"E178");
            var Q6;
            Q6=makeQuery(id+"F1.opExtrude","SWEPT_BODY",BODY,{"disambiguationData":[OSD([sQuery(id+"F0.wireOp",EDGE,"E0.bottom"),sQuery(id+"F0.wireOp",EDGE,"E0.top"),sQuery(id+"F0.wireOp",EDGE,"E0.left"),sQuery(id+"F0.wireOp",EDGE,"E0.right"),sQuery(id+"F0.wireOp",EDGE,"E1"),sQuery(id+"F0.wireOp",EDGE,"E2"),sQuery(id+"F0.wireOp",EDGE,"E5"),sQuery(id+"F0.wireOp",EDGE,"E6"),sQuery(id+"F0.wireOp",EDGE,"E9"),sQuery(id+"F0.wireOp",EDGE,"E10"),sQuery(id+"F0.wireOp",EDGE,"E13.0"),sQuery(id+"F0.wireOp",EDGE,"E14.0"),sQuery(id+"F0.wireOp",EDGE,"E15.0"),sQuery(id+"F0.wireOp",EDGE,"E16.0"),sQuery(id+"F0.wireOp",EDGE,"E17"),sQuery(id+"F0.wireOp",EDGE,"E18"),sQuery(id+"F0.wireOp",EDGE,"E21.trimOffspring"),sQuery(id+"F0.wireOp",EDGE,"E22.0"),sQuery(id+"F0.wireOp",EDGE,"E23.0"),sQuery(id+"F0.wireOp",EDGE,"E24.0"),sQuery(id+"F0.wireOp",EDGE,"E25.0"),sQuery(id+"F0.wireOp",EDGE,"E26"),sQuery(id+"F0.wireOp",EDGE,"E27"),sQuery(id+"F0.wireOp",EDGE,"E30.trimOffspring")])]});
            hole(context, id + "F13", {"style" : HoleStyle.C_BORE, "endStyle" : HoleEndStyle.BLIND, "standardTappedOrClearance" : lookupTablePath({ "standard" : "ISO", "fit" : "Normal", "size" : "M3", "type" : "Clearance" }), "standardBlindInLast" : lookupTablePath({ "fit" : "Standard", "standard" : "ISO", "size" : "M3", "type" : "Clearance" }), "holeDiameter" : 3.3 * mm, "cBoreDiameter" : 6.5 * mm, "cBoreDepth" : 3 * mm, "holeDepth" : 14 * mm, "tappedDepth" : 3 * mm, "tapClearance" : 3, "startFromSketch" : true, "locations" : qUnion([Q0, Q1, Q2, Q3, Q4, Q5]), "scope" : qUnion([Q6])});
        }
        {
            var Q0;
            Q0=makeQuery(id+"F1.opExtrude","SWEPT_FACE",FACE,{"disambiguationData":[OSD([sQuery(id+"F0.wireOp",EDGE,"E16.0")])]});
            var sketch = newSketch(context, id + "F14", { "sketchPlane" : qUnion([Q0])});
            skCircle(sketch, "E184.cCircle", {"center": v(7.5, 26.6) * mm, "radius": 3 * mm, "construction": true});
            skLineSegment(sketch, "E184.0", {"start": v(4.5, 24.87) * mm, "end": v(4.5, 28.33) * mm});
            skLineSegment(sketch, "E184.1", {"start": v(4.5, 28.33) * mm, "end": v(7.5, 30.06) * mm});
            skLineSegment(sketch, "E184.2", {"start": v(7.5, 30.06) * mm, "end": v(10.5, 28.33) * mm});
            skLineSegment(sketch, "E184.3", {"start": v(10.5, 28.33) * mm, "end": v(10.5, 24.87) * mm});
            skLineSegment(sketch, "E184.4", {"start": v(10.5, 24.87) * mm, "end": v(7.5, 23.14) * mm});
            skLineSegment(sketch, "E184.5", {"start": v(7.5, 23.14) * mm, "end": v(4.5, 24.87) * mm});
            skPoint(sketch, "E184.0.midPoint", {"position": v(4.5, 26.6) * mm});
            skCircle(sketch, "E185.cCircle", {"center": v(37.5, 26.6) * mm, "radius": 3 * mm, "construction": true});
            skLineSegment(sketch, "E185.0", {"start": v(34.5, 24.87) * mm, "end": v(34.5, 28.33) * mm});
            skLineSegment(sketch, "E185.1", {"start": v(34.5, 28.33) * mm, "end": v(37.5, 30.06) * mm});
            skLineSegment(sketch, "E185.2", {"start": v(37.5, 30.06) * mm, "end": v(40.5, 28.33) * mm});
            skLineSegment(sketch, "E185.3", {"start": v(40.5, 28.33) * mm, "end": v(40.5, 24.87) * mm});
            skLineSegment(sketch, "E185.4", {"start": v(40.5, 24.87) * mm, "end": v(37.5, 23.14) * mm});
            skLineSegment(sketch, "E185.5", {"start": v(37.5, 23.14) * mm, "end": v(34.5, 24.87) * mm});
            skPoint(sketch, "E185.0.midPoint", {"position": v(34.5, 26.6) * mm});
            skCircle(sketch, "E186.cCircle", {"center": v(22.5, 26.6) * mm, "radius": 3 * mm, "construction": true});
            skLineSegment(sketch, "E186.0", {"start": v(25.5, 28.33) * mm, "end": v(25.5, 24.87) * mm});
            skLineSegment(sketch, "E186.1", {"start": v(25.5, 24.87) * mm, "end": v(22.5, 23.14) * mm});
            skLineSegment(sketch, "E186.2", {"start": v(22.5, 23.14) * mm, "end": v(19.5, 24.87) * mm});
            skLineSegment(sketch, "E186.3", {"start": v(19.5, 24.87) * mm, "end": v(19.5, 28.33) * mm});
            skLineSegment(sketch, "E186.4", {"start": v(19.5, 28.33) * mm, "end": v(22.5, 30.06) * mm});
            skLineSegment(sketch, "E186.5", {"start": v(22.5, 30.06) * mm, "end": v(25.5, 28.33) * mm});
            skPoint(sketch, "E186.0.midPoint", {"position": v(25.5, 26.6) * mm});
            skSolve(sketch);
        }
        {
            var Q0;
            Q0=qSketchRegion(id+"F14",true);
            extrude(context, id + "F15", {"entities" : qUnion([Q0]), "operationType" : NewBodyOperationType.REMOVE, "oppositeDirection" : true, "depth" : 3 * mm});
        }
        {
            var Q0;
            Q0=makeQuery(id+"F1.opExtrude","SWEPT_FACE",FACE,{"disambiguationData":[OSD([sQuery(id+"F0.wireOp",EDGE,"E25.0")])]});
            var sketch = newSketch(context, id + "F16", { "sketchPlane" : qUnion([Q0])});
            skCircle(sketch, "E187.cCircle", {"center": v(37.5, -26.6) * mm, "radius": 3 * mm, "construction": true});
            skLineSegment(sketch, "E187.0", {"start": v(34.5, -28.33) * mm, "end": v(34.5, -24.87) * mm});
            skLineSegment(sketch, "E187.1", {"start": v(34.5, -24.87) * mm, "end": v(37.5, -23.14) * mm});
            skLineSegment(sketch, "E187.2", {"start": v(37.5, -23.14) * mm, "end": v(40.5, -24.87) * mm});
            skLineSegment(sketch, "E187.3", {"start": v(40.5, -24.87) * mm, "end": v(40.5, -28.33) * mm});
            skLineSegment(sketch, "E187.4", {"start": v(40.5, -28.33) * mm, "end": v(37.5, -30.06) * mm});
            skLineSegment(sketch, "E187.5", {"start": v(37.5, -30.06) * mm, "end": v(34.5, -28.33) * mm});
            skPoint(sketch, "E187.0.midPoint", {"position": v(34.5, -26.6) * mm});
            skCircle(sketch, "E188.cCircle", {"center": v(7.5, -26.6) * mm, "radius": 3 * mm, "construction": true});
            skLineSegment(sketch, "E188.0", {"start": v(4.5, -28.33) * mm, "end": v(4.5, -24.87) * mm});
            skLineSegment(sketch, "E188.1", {"start": v(4.5, -24.87) * mm, "end": v(7.5, -23.14) * mm});
            skLineSegment(sketch, "E188.2", {"start": v(7.5, -23.14) * mm, "end": v(10.5, -24.87) * mm});
            skLineSegment(sketch, "E188.3", {"start": v(10.5, -24.87) * mm, "end": v(10.5, -28.33) * mm});
            skLineSegment(sketch, "E188.4", {"start": v(10.5, -28.33) * mm, "end": v(7.5, -30.06) * mm});
            skLineSegment(sketch, "E188.5", {"start": v(7.5, -30.06) * mm, "end": v(4.5, -28.33) * mm});
            skPoint(sketch, "E188.0.midPoint", {"position": v(4.5, -26.6) * mm});
            skCircle(sketch, "E189.cCircle", {"center": v(22.5, -26.6) * mm, "radius": 3 * mm, "construction": true});
            skLineSegment(sketch, "E189.0", {"start": v(19.5, -28.33) * mm, "end": v(19.5, -24.87) * mm});
            skLineSegment(sketch, "E189.1", {"start": v(19.5, -24.87) * mm, "end": v(22.5, -23.14) * mm});
            skLineSegment(sketch, "E189.2", {"start": v(22.5, -23.14) * mm, "end": v(25.5, -24.87) * mm});
            skLineSegment(sketch, "E189.3", {"start": v(25.5, -24.87) * mm, "end": v(25.5, -28.33) * mm});
            skLineSegment(sketch, "E189.4", {"start": v(25.5, -28.33) * mm, "end": v(22.5, -30.06) * mm});
            skLineSegment(sketch, "E189.5", {"start": v(22.5, -30.06) * mm, "end": v(19.5, -28.33) * mm});
            skPoint(sketch, "E189.0.midPoint", {"position": v(19.5, -26.6) * mm});
            skSolve(sketch);
        }
        {
            var Q0;
            Q0=qSketchRegion(id+"F16",true);
            extrude(context, id + "F17", {"entities" : qUnion([Q0]), "operationType" : NewBodyOperationType.REMOVE, "oppositeDirection" : true, "depth" : 3 * mm});
        }
        {
            var Q0;
            Q0=makeQuery(id+"F1.opExtrude","CAP_EDGE",EDGE,{"disambiguationData":[OSD([sQuery(id+"F0.wireOp",EDGE,"E26")])],"isStart":true});
            var Q1;
            Q1=makeQuery(id+"F1.opExtrude","CAP_EDGE",EDGE,{"disambiguationData":[OSD([sQuery(id+"F0.wireOp",EDGE,"E27")])],"isStart":true});
            var Q2;
            Q2=makeQuery(id+"F1.opExtrude","CAP_EDGE",EDGE,{"disambiguationData":[OSD([sQuery(id+"F0.wireOp",EDGE,"E17")])],"isStart":true});
            var Q3;
            Q3=makeQuery(id+"F1.opExtrude","CAP_EDGE",EDGE,{"disambiguationData":[OSD([sQuery(id+"F0.wireOp",EDGE,"E18")])],"isStart":true});
            var Q4;
            Q4=makeQuery(id+"F1.opExtrude","CAP_EDGE",EDGE,{"disambiguationData":[OSD([sQuery(id+"F0.wireOp",EDGE,"E18")])],"isStart":false});
            var Q5;
            Q5=makeQuery(id+"F1.opExtrude","CAP_EDGE",EDGE,{"disambiguationData":[OSD([sQuery(id+"F0.wireOp",EDGE,"E17")])],"isStart":false});
            var Q6;
            Q6=makeQuery(id+"F1.opExtrude","CAP_EDGE",EDGE,{"disambiguationData":[OSD([sQuery(id+"F0.wireOp",EDGE,"E26")])],"isStart":false});
            var Q7;
            Q7=makeQuery(id+"F1.opExtrude","CAP_EDGE",EDGE,{"disambiguationData":[OSD([sQuery(id+"F0.wireOp",EDGE,"E27")])],"isStart":false});
            fillet(context, id + "F18", {"entities" : qUnion([Q0, Q1, Q2, Q3, Q4, Q5, Q6, Q7]), "radius" : 5 * mm, "tangentPropagation" : true, "allowEdgeOverflow" : false});
        }
        {
            var Q0;
            Q0=makeQuery(id+"F1.opExtrude","SWEPT_EDGE",EDGE,{"disambiguationData":[OSD([sQuery(id+"F0.wireOp",EDGE,"E5"),sQuery(id+"F0.wireOp",EDGE,"E25.0")])]});
            var Q1;
            Q1=makeQuery(id+"F1.opExtrude","SWEPT_EDGE",EDGE,{"disambiguationData":[OSD([sQuery(id+"F0.wireOp",EDGE,"E1"),sQuery(id+"F0.wireOp",EDGE,"E23.0")])]});
            var Q2;
            Q2=makeQuery(id+"F1.opExtrude","SWEPT_EDGE",EDGE,{"disambiguationData":[OSD([sQuery(id+"F0.wireOp",EDGE,"E1"),sQuery(id+"F0.wireOp",EDGE,"E22.0")])]});
            var Q3;
            Q3=makeQuery(id+"F1.opExtrude","SWEPT_EDGE",EDGE,{"disambiguationData":[OSD([sQuery(id+"F0.wireOp",EDGE,"E24.0"),sQuery(id+"F0.wireOp",EDGE,"E30.trimOffspring")])]});
            var Q4;
            Q4=makeQuery(id+"F1.opExtrude","SWEPT_EDGE",EDGE,{"disambiguationData":[OSD([sQuery(id+"F0.wireOp",EDGE,"E16.0"),sQuery(id+"F0.wireOp",EDGE,"E21.trimOffspring")])]});
            var Q5;
            Q5=makeQuery(id+"F1.opExtrude","SWEPT_EDGE",EDGE,{"disambiguationData":[OSD([sQuery(id+"F0.wireOp",EDGE,"E2"),sQuery(id+"F0.wireOp",EDGE,"E13.0")])]});
            var Q6;
            Q6=makeQuery(id+"F1.opExtrude","SWEPT_EDGE",EDGE,{"disambiguationData":[OSD([sQuery(id+"F0.wireOp",EDGE,"E2"),sQuery(id+"F0.wireOp",EDGE,"E14.0")])]});
            var Q7;
            Q7=makeQuery(id+"F1.opExtrude","SWEPT_EDGE",EDGE,{"disambiguationData":[OSD([sQuery(id+"F0.wireOp",EDGE,"E6"),sQuery(id+"F0.wireOp",EDGE,"E15.0")])]});
            var Q8;
            Q8=makeQuery(id+"F1.opExtrude","CAP_EDGE",EDGE,{"disambiguationData":[OSD([sQuery(id+"F0.wireOp",EDGE,"E0.bottom")])],"isStart":true});
            var Q9;
            Q9=makeQuery(id+"F1.opExtrude","CAP_EDGE",EDGE,{"disambiguationData":[OSD([sQuery(id+"F0.wireOp",EDGE,"E0.top")])],"isStart":true});
            var Q10;
            Q10=makeQuery(id+"F1.opExtrude","CAP_EDGE",EDGE,{"disambiguationData":[OSD([sQuery(id+"F0.wireOp",EDGE,"E10")])],"isStart":true});
            var Q11;
            Q11=makeQuery(id+"F1.opExtrude","CAP_EDGE",EDGE,{"disambiguationData":[OSD([sQuery(id+"F0.wireOp",EDGE,"E9")])],"isStart":true});
            var Q12;
            Q12=makeQuery(id+"F1.opExtrude","CAP_EDGE",EDGE,{"disambiguationData":[OSD([sQuery(id+"F0.wireOp",EDGE,"E14.0")])],"isStart":true});
            var Q13;
            Q13=makeQuery(id+"F1.opExtrude","CAP_EDGE",EDGE,{"disambiguationData":[OSD([sQuery(id+"F0.wireOp",EDGE,"E13.0")])],"isStart":true});
            var Q14;
            Q14=makeQuery(id+"F1.opExtrude","CAP_EDGE",EDGE,{"disambiguationData":[OSD([sQuery(id+"F0.wireOp",EDGE,"E22.0")])],"isStart":true});
            var Q15;
            Q15=makeQuery(id+"F1.opExtrude","CAP_EDGE",EDGE,{"disambiguationData":[OSD([sQuery(id+"F0.wireOp",EDGE,"E23.0")])],"isStart":true});
            fillet(context, id + "F19", {"entities" : qUnion([Q0, Q1, Q2, Q3, Q4, Q5, Q6, Q7, Q8, Q9, Q10, Q11, Q12, Q13, Q14, Q15]), "radius" : 1 * mm, "tangentPropagation" : true, "allowEdgeOverflow" : false});
        }
        {
            var Q0;
            {var subQ0=sQuery(id+"F0.wireOp",EDGE,"E0.right");Q0=makeQuery(id+"F4.boolean.opBoolean","SPLIT",FACE,{"disambiguationData":[TD([makeQuery(id+"F1.opExtrude","SWEPT_FACE",FACE,{"disambiguationData":[OSD([sQuery(id+"F0.wireOp",EDGE,"E9")])]})])],"derivedFrom":makeQuery(id+"F1.opExtrude","SWEPT_FACE",FACE,{"disambiguationData":[OSD([subQ0])]})});}
            var sketch = newSketch(context, id + "F20", { "sketchPlane" : qUnion([Q0])});
            skLineSegment(sketch, "E190", {"start": v(-44, 27.2) * mm, "end": v(-1, 27.2) * mm, "construction": true});
            skLineSegment(sketch, "E191", {"start": v(-44, 39.7) * mm, "end": v(-1, 39.7) * mm, "construction": true});
            skLineSegment(sketch, "E192", {"start": v(-22.5, 22.2) * mm, "end": v(-22.5, 27.2) * mm, "construction": true});
            skLineSegment(sketch, "E193", {"start": v(-22.5, 27.2) * mm, "end": v(-22.5, 39.7) * mm, "construction": true});
            skCircle(sketch, "E194.cCircle", {"center": v(-37.5, 39.7) * mm, "radius": 3 * mm, "construction": true});
            skLineSegment(sketch, "E194.0", {"start": v(-39.23, 42.7) * mm, "end": v(-35.77, 42.7) * mm});
            skLineSegment(sketch, "E194.1", {"start": v(-35.77, 42.7) * mm, "end": v(-34.04, 39.7) * mm});
            skLineSegment(sketch, "E194.2", {"start": v(-34.04, 39.7) * mm, "end": v(-35.77, 36.7) * mm});
            skLineSegment(sketch, "E194.3", {"start": v(-35.77, 36.7) * mm, "end": v(-39.23, 36.7) * mm});
            skLineSegment(sketch, "E194.4", {"start": v(-39.23, 36.7) * mm, "end": v(-40.96, 39.7) * mm});
            skLineSegment(sketch, "E194.5", {"start": v(-40.96, 39.7) * mm, "end": v(-39.23, 42.7) * mm});
            skPoint(sketch, "E194.0.midPoint", {"position": v(-37.5, 42.7) * mm});
            skCircle(sketch, "E195.cCircle", {"center": v(-30, 39.7) * mm, "radius": 3 * mm, "construction": true});
            skLineSegment(sketch, "E195.0", {"start": v(-31.73, 42.7) * mm, "end": v(-28.27, 42.7) * mm});
            skLineSegment(sketch, "E195.1", {"start": v(-28.27, 42.7) * mm, "end": v(-26.54, 39.7) * mm});
            skLineSegment(sketch, "E195.2", {"start": v(-26.54, 39.7) * mm, "end": v(-28.27, 36.7) * mm});
            skLineSegment(sketch, "E195.3", {"start": v(-28.27, 36.7) * mm, "end": v(-31.73, 36.7) * mm});
            skLineSegment(sketch, "E195.4", {"start": v(-31.73, 36.7) * mm, "end": v(-33.46, 39.7) * mm});
            skLineSegment(sketch, "E195.5", {"start": v(-33.46, 39.7) * mm, "end": v(-31.73, 42.7) * mm});
            skPoint(sketch, "E195.0.midPoint", {"position": v(-30, 42.7) * mm});
            skCircle(sketch, "E196.cCircle", {"center": v(-15, 39.7) * mm, "radius": 3 * mm, "construction": true});
            skLineSegment(sketch, "E196.0", {"start": v(-16.73, 42.7) * mm, "end": v(-13.27, 42.7) * mm});
            skLineSegment(sketch, "E196.1", {"start": v(-13.27, 42.7) * mm, "end": v(-11.54, 39.7) * mm});
            skLineSegment(sketch, "E196.2", {"start": v(-11.54, 39.7) * mm, "end": v(-13.27, 36.7) * mm});
            skLineSegment(sketch, "E196.3", {"start": v(-13.27, 36.7) * mm, "end": v(-16.73, 36.7) * mm});
            skLineSegment(sketch, "E196.4", {"start": v(-16.73, 36.7) * mm, "end": v(-18.46, 39.7) * mm});
            skLineSegment(sketch, "E196.5", {"start": v(-18.46, 39.7) * mm, "end": v(-16.73, 42.7) * mm});
            skPoint(sketch, "E196.0.midPoint", {"position": v(-15, 42.7) * mm});
            skCircle(sketch, "E197.cCircle", {"center": v(-7.5, 39.7) * mm, "radius": 3 * mm, "construction": true});
            skLineSegment(sketch, "E197.0", {"start": v(-9.23, 42.7) * mm, "end": v(-5.77, 42.7) * mm});
            skLineSegment(sketch, "E197.1", {"start": v(-5.77, 42.7) * mm, "end": v(-4.04, 39.7) * mm});
            skLineSegment(sketch, "E197.2", {"start": v(-4.04, 39.7) * mm, "end": v(-5.77, 36.7) * mm});
            skLineSegment(sketch, "E197.3", {"start": v(-5.77, 36.7) * mm, "end": v(-9.23, 36.7) * mm});
            skLineSegment(sketch, "E197.4", {"start": v(-9.23, 36.7) * mm, "end": v(-10.96, 39.7) * mm});
            skLineSegment(sketch, "E197.5", {"start": v(-10.96, 39.7) * mm, "end": v(-9.23, 42.7) * mm});
            skPoint(sketch, "E197.0.midPoint", {"position": v(-7.5, 42.7) * mm});
            skCircle(sketch, "E198.cCircle", {"center": v(-37.5, 27.2) * mm, "radius": 3 * mm, "construction": true});
            skPoint(sketch, "E198.cCircle.centerSnap0", {"position": v(-37.5, 36.7) * mm});
            skLineSegment(sketch, "E198.0", {"start": v(-35.77, 24.2) * mm, "end": v(-39.23, 24.2) * mm});
            skLineSegment(sketch, "E198.1", {"start": v(-39.23, 24.2) * mm, "end": v(-40.96, 27.2) * mm});
            skLineSegment(sketch, "E198.2", {"start": v(-40.96, 27.2) * mm, "end": v(-39.23, 30.2) * mm});
            skLineSegment(sketch, "E198.3", {"start": v(-39.23, 30.2) * mm, "end": v(-35.77, 30.2) * mm});
            skLineSegment(sketch, "E198.4", {"start": v(-35.77, 30.2) * mm, "end": v(-34.04, 27.2) * mm});
            skLineSegment(sketch, "E198.5", {"start": v(-34.04, 27.2) * mm, "end": v(-35.77, 24.2) * mm});
            skPoint(sketch, "E198.0.midPoint", {"position": v(-37.5, 24.2) * mm});
            skCircle(sketch, "E199.cCircle", {"center": v(-30, 27.2) * mm, "radius": 3 * mm, "construction": true});
            skPoint(sketch, "E199.cCircle.centerSnap0", {"position": v(-30, 36.7) * mm});
            skLineSegment(sketch, "E199.0", {"start": v(-28.27, 24.2) * mm, "end": v(-31.73, 24.2) * mm});
            skLineSegment(sketch, "E199.1", {"start": v(-31.73, 24.2) * mm, "end": v(-33.46, 27.2) * mm});
            skLineSegment(sketch, "E199.2", {"start": v(-33.46, 27.2) * mm, "end": v(-31.73, 30.2) * mm});
            skLineSegment(sketch, "E199.3", {"start": v(-31.73, 30.2) * mm, "end": v(-28.27, 30.2) * mm});
            skLineSegment(sketch, "E199.4", {"start": v(-28.27, 30.2) * mm, "end": v(-26.54, 27.2) * mm});
            skLineSegment(sketch, "E199.5", {"start": v(-26.54, 27.2) * mm, "end": v(-28.27, 24.2) * mm});
            skPoint(sketch, "E199.0.midPoint", {"position": v(-30, 24.2) * mm});
            skCircle(sketch, "E200.cCircle", {"center": v(-15, 27.2) * mm, "radius": 3 * mm, "construction": true});
            skPoint(sketch, "E200.cCircle.centerSnap0", {"position": v(-15, 36.7) * mm});
            skLineSegment(sketch, "E200.0", {"start": v(-13.27, 24.2) * mm, "end": v(-16.73, 24.2) * mm});
            skLineSegment(sketch, "E200.1", {"start": v(-16.73, 24.2) * mm, "end": v(-18.46, 27.2) * mm});
            skLineSegment(sketch, "E200.2", {"start": v(-18.46, 27.2) * mm, "end": v(-16.73, 30.2) * mm});
            skLineSegment(sketch, "E200.3", {"start": v(-16.73, 30.2) * mm, "end": v(-13.27, 30.2) * mm});
            skLineSegment(sketch, "E200.4", {"start": v(-13.27, 30.2) * mm, "end": v(-11.54, 27.2) * mm});
            skLineSegment(sketch, "E200.5", {"start": v(-11.54, 27.2) * mm, "end": v(-13.27, 24.2) * mm});
            skPoint(sketch, "E200.0.midPoint", {"position": v(-15, 24.2) * mm});
            skCircle(sketch, "E201.cCircle", {"center": v(-7.5, 27.2) * mm, "radius": 3 * mm, "construction": true});
            skLineSegment(sketch, "E201.0", {"start": v(-5.77, 24.2) * mm, "end": v(-9.23, 24.2) * mm});
            skLineSegment(sketch, "E201.1", {"start": v(-9.23, 24.2) * mm, "end": v(-10.96, 27.2) * mm});
            skLineSegment(sketch, "E201.2", {"start": v(-10.96, 27.2) * mm, "end": v(-9.23, 30.2) * mm});
            skLineSegment(sketch, "E201.3", {"start": v(-9.23, 30.2) * mm, "end": v(-5.77, 30.2) * mm});
            skLineSegment(sketch, "E201.4", {"start": v(-5.77, 30.2) * mm, "end": v(-4.04, 27.2) * mm});
            skLineSegment(sketch, "E201.5", {"start": v(-4.04, 27.2) * mm, "end": v(-5.77, 24.2) * mm});
            skPoint(sketch, "E201.0.midPoint", {"position": v(-7.5, 24.2) * mm});
            skLineSegment(sketch, "E202", {"start": v(-37.5, 39.7) * mm, "end": v(-37.5, 36.7) * mm, "construction": true});
            skLineSegment(sketch, "E203", {"start": v(-30, 39.7) * mm, "end": v(-30, 36.7) * mm, "construction": true});
            skLineSegment(sketch, "E204", {"start": v(-15, 39.7) * mm, "end": v(-15, 36.7) * mm, "construction": true});
            skLineSegment(sketch, "E205", {"start": v(-7.5, 39.7) * mm, "end": v(-7.5, 42.7) * mm, "construction": true});
            skLineSegment(sketch, "E206", {"start": v(-37.5, 27.2) * mm, "end": v(-37.5, 24.2) * mm, "construction": true});
            skLineSegment(sketch, "E207", {"start": v(-30, 27.2) * mm, "end": v(-30, 24.2) * mm, "construction": true});
            skLineSegment(sketch, "E208", {"start": v(-15, 27.2) * mm, "end": v(-15, 24.2) * mm, "construction": true});
            skLineSegment(sketch, "E209", {"start": v(-7.5, 27.2) * mm, "end": v(-7.5, 24.2) * mm, "construction": true});
            skSolve(sketch);
        }
        {
            var Q0;
            Q0=qSketchRegion(id+"F20",true);
            extrude(context, id + "F21", {"entities" : qUnion([Q0]), "operationType" : NewBodyOperationType.REMOVE, "oppositeDirection" : true, "depth" : 3 * mm});
        }
        {
            var Q0;
            {var subQ0=sQuery(id+"F0.wireOp",EDGE,"E0.right");Q0=makeQuery(id+"F4.boolean.opBoolean","SPLIT",FACE,{"disambiguationData":[TD([makeQuery(id+"F1.opExtrude","SWEPT_FACE",FACE,{"disambiguationData":[OSD([sQuery(id+"F0.wireOp",EDGE,"E9")])]})])],"derivedFrom":makeQuery(id+"F1.opExtrude","SWEPT_FACE",FACE,{"disambiguationData":[OSD([subQ0])]})});}
            var sketch = newSketch(context, id + "F22", { "sketchPlane" : qUnion([Q0])});
            skLineSegment(sketch, "E210", {"start": v(-40.96, 39.7) * mm, "end": v(-34.04, 39.7) * mm, "construction": true});
            skLineSegment(sketch, "E211", {"start": v(-34.04, 39.7) * mm, "end": v(-33.46, 39.7) * mm, "construction": true});
            skLineSegment(sketch, "E212", {"start": v(-33.46, 39.7) * mm, "end": v(-26.54, 39.7) * mm, "construction": true});
            skLineSegment(sketch, "E213", {"start": v(-26.54, 39.7) * mm, "end": v(-18.46, 39.7) * mm, "construction": true});
            skLineSegment(sketch, "E214", {"start": v(-10.96, 39.7) * mm, "end": v(-4.04, 39.7) * mm, "construction": true});
            skLineSegment(sketch, "E215", {"start": v(-40.96, 27.2) * mm, "end": v(-34.04, 27.2) * mm, "construction": true});
            skLineSegment(sketch, "E216", {"start": v(-34.04, 27.2) * mm, "end": v(-33.46, 27.2) * mm, "construction": true});
            skLineSegment(sketch, "E217", {"start": v(-33.46, 27.2) * mm, "end": v(-26.54, 27.2) * mm, "construction": true});
            skLineSegment(sketch, "E218", {"start": v(-26.54, 27.2) * mm, "end": v(-18.46, 27.2) * mm, "construction": true});
            skLineSegment(sketch, "E219", {"start": v(-18.46, 27.2) * mm, "end": v(-11.54, 27.2) * mm, "construction": true});
            skLineSegment(sketch, "E220", {"start": v(-11.54, 27.2) * mm, "end": v(-10.96, 27.2) * mm, "construction": true});
            skLineSegment(sketch, "E221", {"start": v(-10.96, 27.2) * mm, "end": v(-4.04, 27.2) * mm, "construction": true});
            skCircle(sketch, "E222", {"center": v(-37.5, 39.7) * mm, "radius": 1.65 * mm});
            skCircle(sketch, "E223", {"center": v(-30, 39.7) * mm, "radius": 1.65 * mm});
            skLineSegment(sketch, "E224", {"start": v(-18.46, 39.7) * mm, "end": v(-11.54, 39.7) * mm, "construction": true});
            skLineSegment(sketch, "E225", {"start": v(-11.54, 39.7) * mm, "end": v(-10.96, 39.7) * mm, "construction": true});
            skCircle(sketch, "E226", {"center": v(-15, 39.7) * mm, "radius": 1.65 * mm});
            skCircle(sketch, "E227", {"center": v(-7.5, 39.7) * mm, "radius": 1.65 * mm});
            skCircle(sketch, "E228", {"center": v(-7.5, 27.2) * mm, "radius": 1.65 * mm});
            skCircle(sketch, "E229", {"center": v(-15, 27.2) * mm, "radius": 1.65 * mm});
            skCircle(sketch, "E230", {"center": v(-30, 27.2) * mm, "radius": 1.65 * mm});
            skCircle(sketch, "E231", {"center": v(-37.5, 27.2) * mm, "radius": 1.65 * mm});
            skSolve(sketch);
        }
        {
            var Q0;
            Q0=qSketchRegion(id+"F22",true);
            extrude(context, id + "F23", {"entities" : qUnion([Q0]), "operationType" : NewBodyOperationType.REMOVE, "endBound" : BoundingType.THROUGH_ALL, "oppositeDirection" : true, "depth" : 25 * mm});
        }
    });
